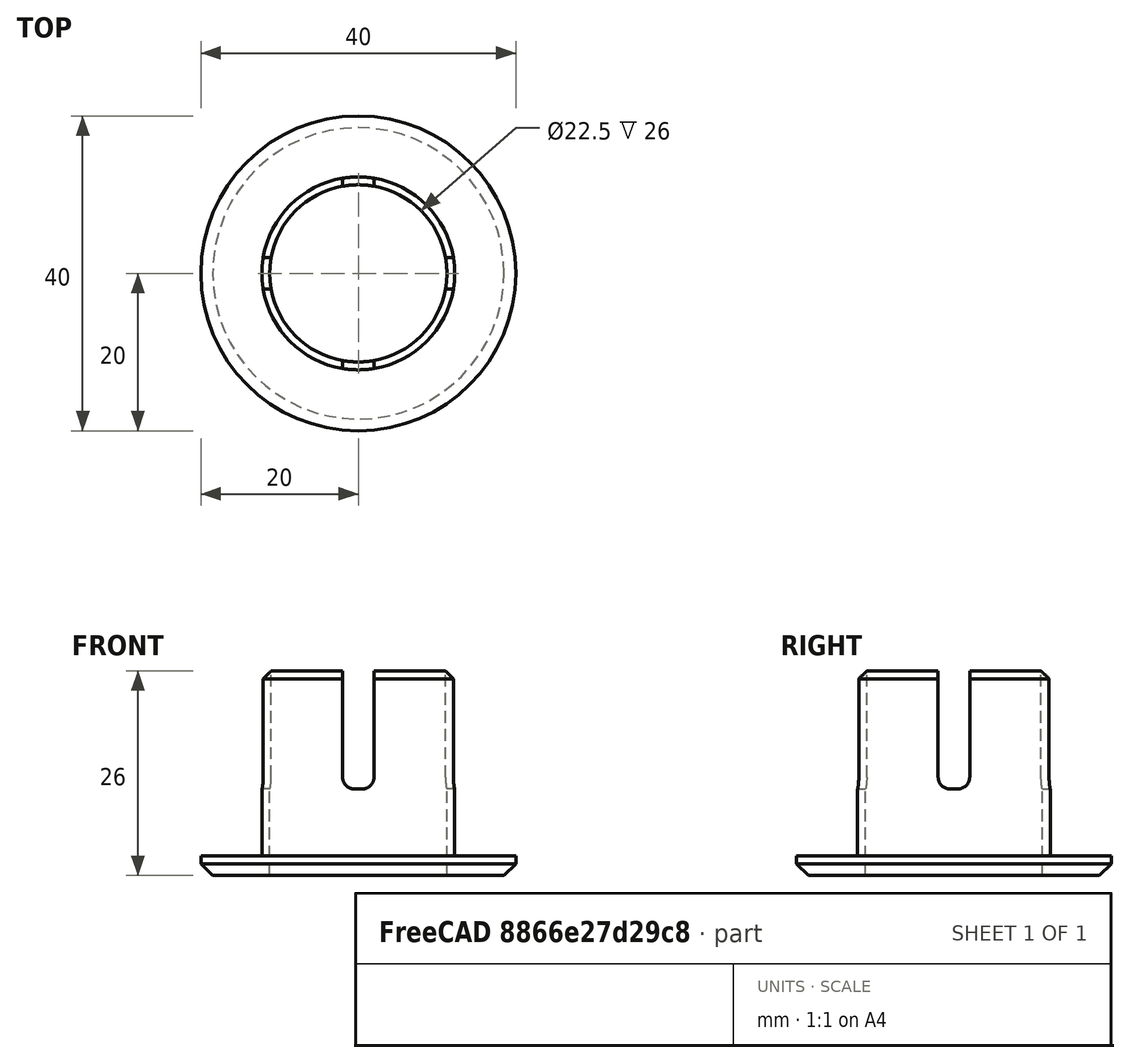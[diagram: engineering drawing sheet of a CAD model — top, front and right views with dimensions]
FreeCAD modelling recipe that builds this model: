
FCSTD DOCUMENT  (FreeCAD 0.16R6712 (Git))
Label: drafting-table-surface
License: All rights reserved
LicenseURL: http://en.wikipedia.org/wiki/All_rights_reserved
objects: Part::Fillet×4, Part::Cylinder×3, Part::Chamfer×2, Part::Fuse×2, Part::Cut×2, Part::Box×2
note: 15 computed .brp shape members not serialized (recipe doc carries the construction recipe); baked Part::Feature solids carry a one-line shape summary decoded from their .brp

FEATURE [Part::Cylinder] Cylinder
  Angle = 360
  Height = 30
  Placement = pos=(0,0,-2) rot=(0,0,1;0rad)
  Radius = 11.25
FEATURE [Part::Cylinder] Cylinder001
  Angle = 360
  Height = 2.5
  Placement = pos=(0,0,-1) rot=(0,0,1;0rad)
  Radius = 20
FEATURE [Part::Cylinder] Cylinder002
  Angle = 360
  Height = 25
  Radius = 12.25
FEATURE [Part::Chamfer] Chamfer
  Base = -> Cylinder001
  Edges = 1 edges r=1.5: [Edge3]
FEATURE [Part::Chamfer] Chamfer001
  Base = -> Cylinder002
  Edges = 1 edges r=1: [Edge1]
FEATURE [Part::Fuse] Fusion
  Base = -> Chamfer
  Tool = -> Chamfer001
FEATURE [Part::Cut] Cut
  Base = -> Fusion
  Tool = -> Cylinder
FEATURE [Part::Box] Box  label="Cube"
  Height = 20
  Length = 4
  Placement = pos=(-2,-15,10) rot=(0,0,1;0rad)
  Width = 30
FEATURE [Part::Fillet] Fillet
  Base = -> Box
  Edges = 1 edges r=1.5: [Edge8]
FEATURE [Part::Fillet] Fillet001
  Base = -> Fillet
  Edges = 1 edges r=1.5: [Edge15]
FEATURE [Part::Box] Box001  label="Cube001"
  Height = 20
  Length = 4
  Placement = pos=(-2,-15,10) rot=(0,0,1;0rad)
  Width = 30
FEATURE [Part::Fillet] Fillet002
  Base = -> Box001
  Edges = 1 edges r=1.5: [Edge8]
FEATURE [Part::Fillet] Fillet003
  Base = -> Fillet002
  Edges = 1 edges r=1.5: [Edge15]
  Placement = pos=(0,0,0) rot=(0,0,1;1.5708rad)
FEATURE [Part::Fuse] Fusion001
  Base = -> Fillet001
  Tool = -> Fillet003
FEATURE [Part::Cut] Cut001  label="grommet"
  Base = -> Cut
  Tool = -> Fusion001
